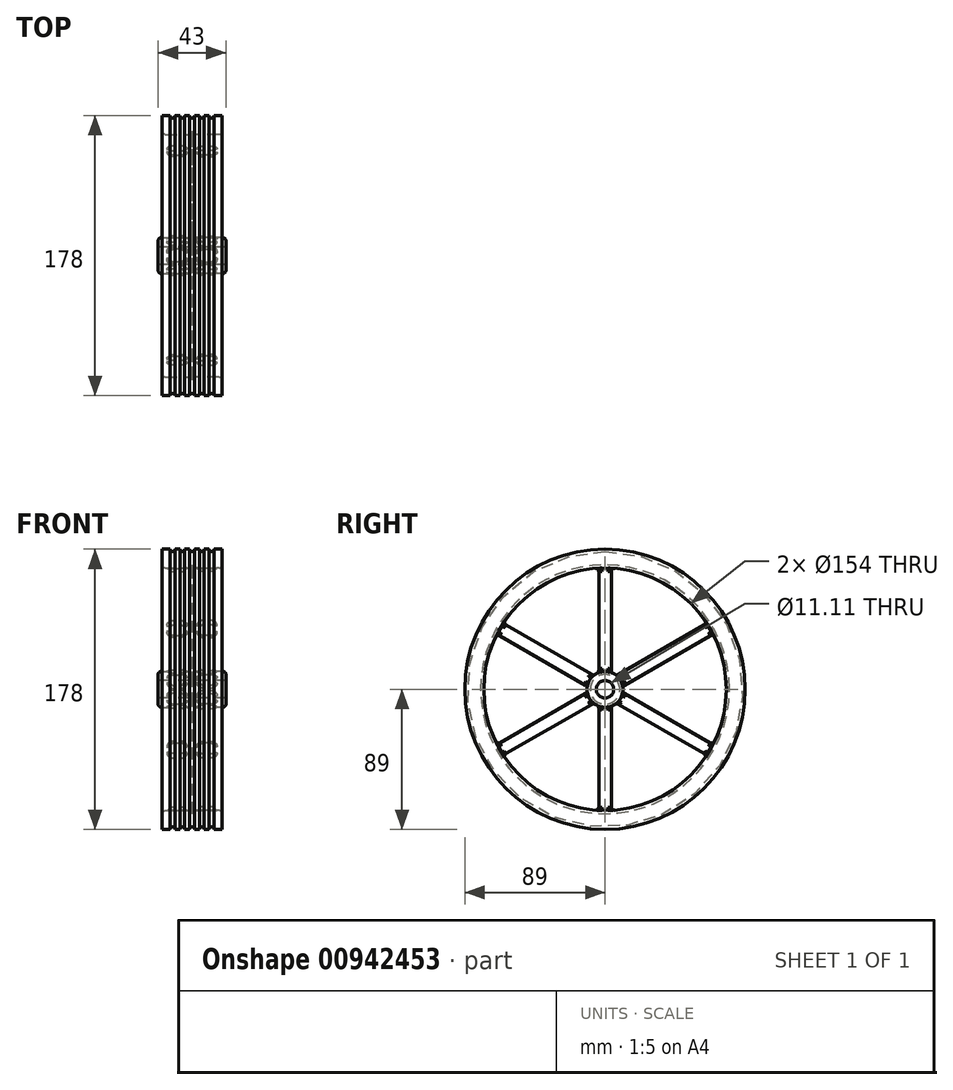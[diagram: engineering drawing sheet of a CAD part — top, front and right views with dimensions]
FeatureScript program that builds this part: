
annotation { "Feature Type Name" : "Feature", "Feature Type Description" : "" }
export const myFeature = defineFeature(function(context is Context, id is Id, definition is map)
    precondition{}
    {
        {
            var Q0;
            Q0=qCreatedBy(makeId("Front.planeOp"),FACE);
            var sketch = newSketch(context, id + "F0", { "sketchPlane" : qUnion([Q0])});
            skLineSegment(sketch, "E0", {"start": v(0, 0) * mm, "end": v(21.5, 0) * mm, "construction": true});
            skLineSegment(sketch, "E1.bottom", {"start": v(0, 11.43) * mm, "end": v(5.03, 11.43) * mm});
            skLineSegment(sketch, "E1.top", {"start": v(0, 5.56) * mm, "end": v(21.5, 5.56) * mm});
            skLineSegment(sketch, "E1.left", {"start": v(0, 11.43) * mm, "end": v(0, 5.56) * mm});
            skLineSegment(sketch, "E1.right", {"start": v(21.5, 11.43) * mm, "end": v(21.5, 5.56) * mm});
            skLineSegment(sketch, "E2.bottom", {"start": v(1.55, 89) * mm, "end": v(4.65, 89) * mm});
            skLineSegment(sketch, "E2.top", {"start": v(0, 77) * mm, "end": v(5.03, 77) * mm});
            skLineSegment(sketch, "E2.left", {"start": v(0, 87.45) * mm, "end": v(0, 77) * mm});
            skLineSegment(sketch, "E2.right", {"start": v(19.05, 89) * mm, "end": v(19.05, 77) * mm});
            skArc(sketch, "E3", {"start": v(0, 87.45) * mm, "mid": v(1.1, 87.9) * mm, "end": v(1.55, 89) * mm});
            skArc(sketch, "E4", {"start": v(4.65, 89) * mm, "mid": v(6.2, 87.45) * mm, "end": v(7.75, 89) * mm});
            skArc(sketch, "E5", {"start": v(10.85, 89) * mm, "mid": v(12.4, 87.45) * mm, "end": v(13.95, 89) * mm});
            skLineSegment(sketch, "E6.trimOffspring", {"start": v(7.75, 89) * mm, "end": v(10.85, 89) * mm});
            skLineSegment(sketch, "E7.trimOffspring", {"start": v(13.95, 89) * mm, "end": v(19.05, 89) * mm});
            skLineSegment(sketch, "E8", {"start": v(9.52, 77) * mm, "end": v(9.52, 11.43) * mm, "construction": true});
            skLineSegment(sketch, "E9", {"start": v(5.03, 77) * mm, "end": v(5.03, 11.43) * mm});
            skLineSegment(sketch, "E10", {"start": v(14.03, 77) * mm, "end": v(14.03, 11.43) * mm});
            skLineSegment(sketch, "E11.trimOffspring", {"start": v(14.03, 77) * mm, "end": v(19.05, 77) * mm});
            skLineSegment(sketch, "E12.trimOffspring", {"start": v(14.03, 11.43) * mm, "end": v(21.5, 11.43) * mm});
            skSolve(sketch);
        }
        {
            var Q0;
            Q0 = qSketchRegion(id + "F0", true);
            var Q1;
            Q1=sQuery(id+"F0.wireOp",EDGE,"E0");
            revolve(context, id + "F1", {"surfaceOperationType" : NewSurfaceOperationType.NEW, "entities" : qUnion([Q0]), "axis" : qUnion([Q1]), "revolveType" : RevolveType.FULL});
        }
        {
            var Q0;
            Q0=qCreatedBy(makeId("Right.planeOp"),FACE);
            var sketch = newSketch(context, id + "F2", { "sketchPlane" : qUnion([Q0])});
            skLineSegment(sketch, "E13", {"start": v(0, 0) * mm, "end": v(0, 77.24) * mm, "construction": true});
            skLineSegment(sketch, "E14", {"start": v(0, 0) * mm, "end": v(66.68, 38.5) * mm, "construction": true});
            skLineSegment(sketch, "E15", {"start": v(0, 0) * mm, "end": v(66.68, -38.5) * mm, "construction": true});
            skArc(sketch, "E16.0", {"start": v(11.27, -1.89) * mm, "mid": v(11.43, 0) * mm, "end": v(11.27, 1.89) * mm});
            skLineSegment(sketch, "E17", {"start": v(11.27, 1.89) * mm, "end": v(68.6, 34.98) * mm});
            skLineSegment(sketch, "E18", {"start": v(68.6, -34.98) * mm, "end": v(11.27, -1.89) * mm});
            skArc(sketch, "E19.trimOffspring", {"start": v(68.6, -34.98) * mm, "mid": v(77, 0) * mm, "end": v(68.6, 34.98) * mm});
            skArc(sketch, "E20.1.0", {"start": v(64.6, 41.91) * mm, "mid": v(38.5, 66.68) * mm, "end": v(4, 76.9) * mm});
            skLineSegment(sketch, "E20.1.1", {"start": v(4, 10.7) * mm, "end": v(4, 76.9) * mm});
            skLineSegment(sketch, "E20.1.2", {"start": v(64.6, 41.91) * mm, "end": v(7.27, 8.82) * mm});
            skArc(sketch, "E20.1.3", {"start": v(7.27, 8.82) * mm, "mid": v(5.72, 9.9) * mm, "end": v(4, 10.7) * mm});
            skArc(sketch, "E20.2.0", {"start": v(-4, 76.9) * mm, "mid": v(-38.5, 66.68) * mm, "end": v(-64.6, 41.91) * mm});
            skLineSegment(sketch, "E20.2.1", {"start": v(-7.27, 8.82) * mm, "end": v(-64.6, 41.91) * mm});
            skLineSegment(sketch, "E20.2.2", {"start": v(-4, 76.9) * mm, "end": v(-4, 10.7) * mm});
            skArc(sketch, "E20.2.3", {"start": v(-4, 10.7) * mm, "mid": v(-5.71, 9.9) * mm, "end": v(-7.27, 8.82) * mm});
            skArc(sketch, "E20.3.0", {"start": v(-68.6, 34.98) * mm, "mid": v(-77, 0) * mm, "end": v(-68.6, -34.98) * mm});
            skLineSegment(sketch, "E20.3.1", {"start": v(-11.27, -1.89) * mm, "end": v(-68.6, -34.98) * mm});
            skLineSegment(sketch, "E20.3.2", {"start": v(-68.6, 34.98) * mm, "end": v(-11.27, 1.89) * mm});
            skArc(sketch, "E20.3.3", {"start": v(-11.27, 1.89) * mm, "mid": v(-11.43, 0) * mm, "end": v(-11.27, -1.89) * mm});
            skArc(sketch, "E20.4.0", {"start": v(-64.6, -41.91) * mm, "mid": v(-38.5, -66.68) * mm, "end": v(-4, -76.9) * mm});
            skLineSegment(sketch, "E20.4.1", {"start": v(-4, -10.7) * mm, "end": v(-4, -76.9) * mm});
            skLineSegment(sketch, "E20.4.2", {"start": v(-64.6, -41.91) * mm, "end": v(-7.27, -8.82) * mm});
            skArc(sketch, "E20.4.3", {"start": v(-7.27, -8.82) * mm, "mid": v(-5.72, -9.9) * mm, "end": v(-4, -10.7) * mm});
            skArc(sketch, "E20.5.0", {"start": v(4, -76.9) * mm, "mid": v(38.5, -66.68) * mm, "end": v(64.6, -41.91) * mm});
            skLineSegment(sketch, "E20.5.1", {"start": v(7.27, -8.82) * mm, "end": v(64.6, -41.91) * mm});
            skLineSegment(sketch, "E20.5.2", {"start": v(4, -76.9) * mm, "end": v(4, -10.7) * mm});
            skArc(sketch, "E20.5.3", {"start": v(4, -10.7) * mm, "mid": v(5.72, -9.9) * mm, "end": v(7.27, -8.82) * mm});
            skSolve(sketch);
        }
        {
            var Q0;
            Q0 = qSketchRegion(id + "F2", true);
            extrude(context, id + "F3", {"entities" : qUnion([Q0]), "operationType" : NewBodyOperationType.REMOVE, "endBound" : BoundingType.THROUGH_ALL, "depth" : 25 * mm, "offsetDistance" : 25 * mm});
        }
        {
            var Q0;
            Q0=makeQuery(id+"F3.boolean.opBoolean","MERGE",FACE,{"derivedFrom":[makeQuery(id+"F1.opRevolve","SWEPT_FACE",FACE,{"disambiguationData":[OSD([sQuery(id+"F0.wireOp",EDGE,"E2.top")])]}),makeQuery(id+"F1.opRevolve","SWEPT_FACE",FACE,{"disambiguationData":[OSD([sQuery(id+"F0.wireOp",EDGE,"E11.trimOffspring")])]})],"fromTools":[makeQuery(id+"F3.opExtrude","SWEPT_FACE",FACE,{"disambiguationData":[OSD([sQuery(id+"F2.wireOp",EDGE,"E19.trimOffspring")])]}),makeQuery(id+"F3.opExtrude","SWEPT_FACE",FACE,{"disambiguationData":[OSD([sQuery(id+"F2.wireOp",EDGE,"E20.1.0")])]}),makeQuery(id+"F3.opExtrude","SWEPT_FACE",FACE,{"disambiguationData":[OSD([sQuery(id+"F2.wireOp",EDGE,"E20.2.0")])]}),makeQuery(id+"F3.opExtrude","SWEPT_FACE",FACE,{"disambiguationData":[OSD([sQuery(id+"F2.wireOp",EDGE,"E20.3.0")])]}),makeQuery(id+"F3.opExtrude","SWEPT_FACE",FACE,{"disambiguationData":[OSD([sQuery(id+"F2.wireOp",EDGE,"E20.4.0")])]}),makeQuery(id+"F3.opExtrude","SWEPT_FACE",FACE,{"disambiguationData":[OSD([sQuery(id+"F2.wireOp",EDGE,"E20.5.0")])]})]});
            var Q1;
            Q1=makeQuery(id+"F3.boolean.opBoolean","SPLIT",FACE,{"disambiguationData":[TD([makeQuery(id+"F3.opExtrude","SWEPT_FACE",FACE,{"disambiguationData":[OSD([sQuery(id+"F2.wireOp",EDGE,"E20.2.1")])]})])],"derivedFrom":makeQuery(id+"F1.opRevolve","SWEPT_FACE",FACE,{"disambiguationData":[OSD([sQuery(id+"F0.wireOp",EDGE,"E10")])]})});
            var Q2;
            Q2=makeQuery(id+"F3.boolean.opBoolean","SPLIT",FACE,{"disambiguationData":[TD([makeQuery(id+"F3.opExtrude","SWEPT_FACE",FACE,{"disambiguationData":[OSD([sQuery(id+"F2.wireOp",EDGE,"E20.1.1")])]})])],"derivedFrom":makeQuery(id+"F1.opRevolve","SWEPT_FACE",FACE,{"disambiguationData":[OSD([sQuery(id+"F0.wireOp",EDGE,"E10")])]})});
            var Q3;
            Q3=makeQuery(id+"F3.boolean.opBoolean","SPLIT",FACE,{"disambiguationData":[TD([makeQuery(id+"F3.opExtrude","SWEPT_FACE",FACE,{"disambiguationData":[OSD([sQuery(id+"F2.wireOp",EDGE,"E17")])]})])],"derivedFrom":makeQuery(id+"F1.opRevolve","SWEPT_FACE",FACE,{"disambiguationData":[OSD([sQuery(id+"F0.wireOp",EDGE,"E10")])]})});
            var Q4;
            Q4=makeQuery(id+"F3.boolean.opBoolean","SPLIT",FACE,{"disambiguationData":[TD([makeQuery(id+"F3.opExtrude","SWEPT_FACE",FACE,{"disambiguationData":[OSD([sQuery(id+"F2.wireOp",EDGE,"E18")])]})])],"derivedFrom":makeQuery(id+"F1.opRevolve","SWEPT_FACE",FACE,{"disambiguationData":[OSD([sQuery(id+"F0.wireOp",EDGE,"E10")])]})});
            var Q5;
            Q5=makeQuery(id+"F3.boolean.opBoolean","SPLIT",FACE,{"disambiguationData":[TD([makeQuery(id+"F3.opExtrude","SWEPT_FACE",FACE,{"disambiguationData":[OSD([sQuery(id+"F2.wireOp",EDGE,"E20.4.1")])]})])],"derivedFrom":makeQuery(id+"F1.opRevolve","SWEPT_FACE",FACE,{"disambiguationData":[OSD([sQuery(id+"F0.wireOp",EDGE,"E10")])]})});
            var Q6;
            Q6=makeQuery(id+"F3.boolean.opBoolean","SPLIT",FACE,{"disambiguationData":[TD([makeQuery(id+"F3.opExtrude","SWEPT_FACE",FACE,{"disambiguationData":[OSD([sQuery(id+"F2.wireOp",EDGE,"E20.3.1")])]})])],"derivedFrom":makeQuery(id+"F1.opRevolve","SWEPT_FACE",FACE,{"disambiguationData":[OSD([sQuery(id+"F0.wireOp",EDGE,"E10")])]})});
            var Q7;
            Q7=makeQuery(id+"F3.boolean.opBoolean","MERGE",FACE,{"derivedFrom":[makeQuery(id+"F1.opRevolve","SWEPT_FACE",FACE,{"disambiguationData":[OSD([sQuery(id+"F0.wireOp",EDGE,"E1.bottom")])]}),makeQuery(id+"F1.opRevolve","SWEPT_FACE",FACE,{"disambiguationData":[OSD([sQuery(id+"F0.wireOp",EDGE,"E12.trimOffspring")])]})],"fromTools":[makeQuery(id+"F3.opExtrude","SWEPT_FACE",FACE,{"disambiguationData":[OSD([sQuery(id+"F2.wireOp",EDGE,"E16.0")])]}),makeQuery(id+"F3.opExtrude","SWEPT_FACE",FACE,{"disambiguationData":[OSD([sQuery(id+"F2.wireOp",EDGE,"E20.1.3")])]}),makeQuery(id+"F3.opExtrude","SWEPT_FACE",FACE,{"disambiguationData":[OSD([sQuery(id+"F2.wireOp",EDGE,"E20.2.3")])]}),makeQuery(id+"F3.opExtrude","SWEPT_FACE",FACE,{"disambiguationData":[OSD([sQuery(id+"F2.wireOp",EDGE,"E20.3.3")])]}),makeQuery(id+"F3.opExtrude","SWEPT_FACE",FACE,{"disambiguationData":[OSD([sQuery(id+"F2.wireOp",EDGE,"E20.4.3")])]}),makeQuery(id+"F3.opExtrude","SWEPT_FACE",FACE,{"disambiguationData":[OSD([sQuery(id+"F2.wireOp",EDGE,"E20.5.3")])]})]});
            var Q8;
            Q8=makeQuery(id+"F3.boolean.opBoolean","SPLIT",FACE,{"disambiguationData":[TD([makeQuery(id+"F3.opExtrude","SWEPT_FACE",FACE,{"disambiguationData":[OSD([sQuery(id+"F2.wireOp",EDGE,"E18")])]})])],"derivedFrom":makeQuery(id+"F1.opRevolve","SWEPT_FACE",FACE,{"disambiguationData":[OSD([sQuery(id+"F0.wireOp",EDGE,"E9")])]})});
            var Q9;
            Q9=makeQuery(id+"F3.boolean.opBoolean","SPLIT",FACE,{"disambiguationData":[TD([makeQuery(id+"F3.opExtrude","SWEPT_FACE",FACE,{"disambiguationData":[OSD([sQuery(id+"F2.wireOp",EDGE,"E20.4.1")])]})])],"derivedFrom":makeQuery(id+"F1.opRevolve","SWEPT_FACE",FACE,{"disambiguationData":[OSD([sQuery(id+"F0.wireOp",EDGE,"E9")])]})});
            var Q10;
            Q10=makeQuery(id+"F3.boolean.opBoolean","SPLIT",FACE,{"disambiguationData":[TD([makeQuery(id+"F3.opExtrude","SWEPT_FACE",FACE,{"disambiguationData":[OSD([sQuery(id+"F2.wireOp",EDGE,"E20.3.1")])]})])],"derivedFrom":makeQuery(id+"F1.opRevolve","SWEPT_FACE",FACE,{"disambiguationData":[OSD([sQuery(id+"F0.wireOp",EDGE,"E9")])]})});
            var Q11;
            Q11=makeQuery(id+"F3.boolean.opBoolean","SPLIT",FACE,{"disambiguationData":[TD([makeQuery(id+"F3.opExtrude","SWEPT_FACE",FACE,{"disambiguationData":[OSD([sQuery(id+"F2.wireOp",EDGE,"E17")])]})])],"derivedFrom":makeQuery(id+"F1.opRevolve","SWEPT_FACE",FACE,{"disambiguationData":[OSD([sQuery(id+"F0.wireOp",EDGE,"E9")])]})});
            var Q12;
            Q12=makeQuery(id+"F3.boolean.opBoolean","SPLIT",FACE,{"disambiguationData":[TD([makeQuery(id+"F3.opExtrude","SWEPT_FACE",FACE,{"disambiguationData":[OSD([sQuery(id+"F2.wireOp",EDGE,"E20.1.1")])]})])],"derivedFrom":makeQuery(id+"F1.opRevolve","SWEPT_FACE",FACE,{"disambiguationData":[OSD([sQuery(id+"F0.wireOp",EDGE,"E9")])]})});
            var Q13;
            Q13=makeQuery(id+"F3.boolean.opBoolean","SPLIT",FACE,{"disambiguationData":[TD([makeQuery(id+"F3.opExtrude","SWEPT_FACE",FACE,{"disambiguationData":[OSD([sQuery(id+"F2.wireOp",EDGE,"E20.2.1")])]})])],"derivedFrom":makeQuery(id+"F1.opRevolve","SWEPT_FACE",FACE,{"disambiguationData":[OSD([sQuery(id+"F0.wireOp",EDGE,"E9")])]})});
            fillet(context, id + "F4", {"entities" : qUnion([Q0, Q1, Q2, Q3, Q4, Q5, Q6, Q7, Q8, Q9, Q10, Q11, Q12, Q13]), "radius" : 2 * mm, "tangentPropagation" : true, "allowEdgeOverflow" : false});
        }
        {
            var Q0;
            Q0=makeQuery(id+"F1.opRevolve","SWEPT_BODY",BODY,{"disambiguationData":[OSD([sQuery(id+"F0.wireOp",EDGE,"E1.bottom"),sQuery(id+"F0.wireOp",EDGE,"E1.top"),sQuery(id+"F0.wireOp",EDGE,"E1.left"),sQuery(id+"F0.wireOp",EDGE,"E1.right"),sQuery(id+"F0.wireOp",EDGE,"E2.bottom"),sQuery(id+"F0.wireOp",EDGE,"E2.top"),sQuery(id+"F0.wireOp",EDGE,"E2.left"),sQuery(id+"F0.wireOp",EDGE,"E2.right"),sQuery(id+"F0.wireOp",EDGE,"E3"),sQuery(id+"F0.wireOp",EDGE,"E4"),sQuery(id+"F0.wireOp",EDGE,"E5"),sQuery(id+"F0.wireOp",EDGE,"E6.trimOffspring"),sQuery(id+"F0.wireOp",EDGE,"E7.trimOffspring"),sQuery(id+"F0.wireOp",EDGE,"E9"),sQuery(id+"F0.wireOp",EDGE,"E10"),sQuery(id+"F0.wireOp",EDGE,"E11.trimOffspring"),sQuery(id+"F0.wireOp",EDGE,"E12.trimOffspring")])]});
            var Q1;
            Q1=qCreatedBy(makeId("Right.planeOp"),FACE);
            mirror(context, id + "F5", {"operationType" : NewBodyOperationType.ADD, "entities" : qUnion([Q0]), "mirrorPlane" : qUnion([Q1])});
        }
    });
